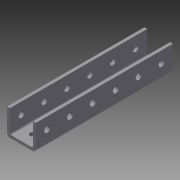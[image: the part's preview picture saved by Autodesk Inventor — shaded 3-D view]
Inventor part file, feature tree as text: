
AUTODESK INVENTOR PART (.ipt)
format: ipt  version: 2014 (Build 180170000, 170)  size: 125,440 bytes
history: native  units: in
note: dims shown in document units (in); Inventor stores cm internally (conversion verified against a paired STEP export)
features: sketch x3, hole x2, extrude x1, pattern_linear x1
ambient origin geometry x8: Origin, YZ Plane, XZ Plane, XY Plane, X Axis, Y Axis, Z Axis, Center Point
bodies: Solid1 (feature_tree)
feature tree (7):
  extrude  "Extrusion1"  Depth=6.0in TaperAngle=0.0deg
  sketch  "Sketch2"  dims[d6=0.5in d7=0.5in]
  sketch  "Sketch3"  dims[d8=0.25in d9=0.75in d10=0.375in d11=0.25in d12=0.5635in d13=1.0in d14=0.8108in d15=0.25in d16=0.75in d17=0.375in d18=0.25in d19=0.5635in d20=1.0in d21=0.8108in d22=2.3622in d24=1.0in]
  hole  "Hole1"  [1 undecoded]
  hole  "Hole2"  [1 undecoded]
  pattern_linear  "Rectangular Pattern1"  [2 undecoded]
  sketch  "Sketch1"  dims[d0=1.25in d1=1.125in d2=0.0625in d3=0.125in d4=6.0in d5=0.0in]
note: 4 required parameter values undecoded (feature->parameter linkage not recoverable at this tier; creation-order binding heuristic only, values carry confidence <= 0.55)
